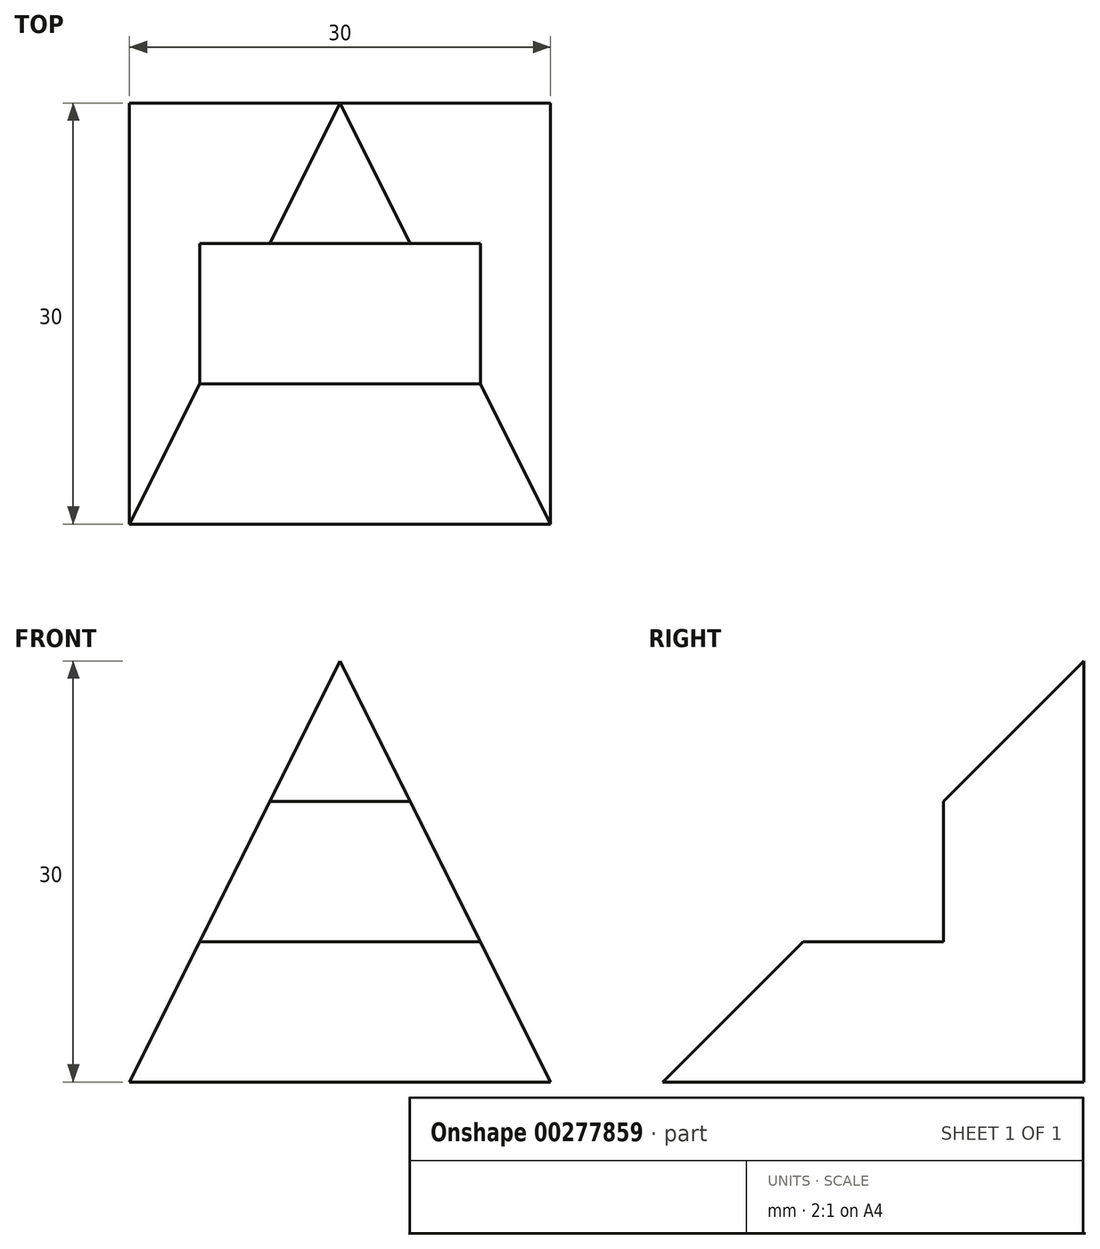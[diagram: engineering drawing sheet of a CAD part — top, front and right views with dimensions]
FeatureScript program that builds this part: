
annotation { "Feature Type Name" : "Feature", "Feature Type Description" : "" }
export const myFeature = defineFeature(function(context is Context, id is Id, definition is map)
    precondition{}
    {
        {
            var Q0;
            Q0=qCreatedBy(makeId("Front.planeOp"),FACE);
            var sketch = newSketch(context, id + "F0", { "sketchPlane" : qUnion([Q0])});
            skLineSegment(sketch, "E0.bottom", {"start": v(-15, 0) * mm, "end": v(15, 0) * mm});
            skLineSegment(sketch, "E0.top", {"start": v(-15, 30) * mm, "end": v(15, 30) * mm});
            skLineSegment(sketch, "E0.left", {"start": v(-15, 0) * mm, "end": v(-15, 30) * mm});
            skLineSegment(sketch, "E0.right", {"start": v(15, 0) * mm, "end": v(15, 30) * mm});
            skLineSegment(sketch, "E1", {"start": v(-15, 0) * mm, "end": v(0, 30) * mm});
            skLineSegment(sketch, "E2", {"start": v(0, 30) * mm, "end": v(15, 0) * mm});
            skSolve(sketch);
        }
        {
            var Q0;
            Q0=makeQuery(id+"F0.imprint","IMPRINT",FACE,{"disambiguationData":[TD([[makeQuery(id+"F0.imprint","IMPRINT",EDGE,{"derivedFrom":sQuery(id+"F0.wireOp",EDGE,"E0.bottom")}),1.0]])]});
            extrude(context, id + "F1", {"entities" : qUnion([Q0]), "depth" : 30 * mm});
        }
        {
            var Q0;
            Q0=qCreatedBy(makeId("Right.planeOp"),FACE);
            var sketch = newSketch(context, id + "F2", { "sketchPlane" : qUnion([Q0])});
            skLineSegment(sketch, "E3.0", {"start": v(-30, 30) * mm, "end": v(0, 30) * mm});
            skLineSegment(sketch, "E4.0", {"start": v(-30, 30) * mm, "end": v(-30, 0) * mm});
            skLineSegment(sketch, "E5", {"start": v(0, 30) * mm, "end": v(-30, 0) * mm});
            skLineSegment(sketch, "E6.bottom", {"start": v(-20, 10) * mm, "end": v(-10, 10) * mm});
            skLineSegment(sketch, "E6.top", {"start": v(-20, 20) * mm, "end": v(-10, 20) * mm});
            skLineSegment(sketch, "E6.left", {"start": v(-20, 10) * mm, "end": v(-20, 20) * mm});
            skLineSegment(sketch, "E6.right", {"start": v(-10, 10) * mm, "end": v(-10, 20) * mm});
            skSolve(sketch);
        }
        {
            var Q0;
            {var subQ3=sQuery(id+"F2.wireOp",EDGE,"E3.0");Q0=makeQuery(id+"F2.imprint","IMPRINT",FACE,{"disambiguationData":[TD([[makeQuery(id+"F2.imprint","IMPRINT",EDGE,{"derivedFrom":subQ3}),-1.0]])]});}
            var Q1;
            {var subQ2=sQuery(id+"F2.wireOp",EDGE,"E6.top");Q1=makeQuery(id+"F2.imprint","IMPRINT",FACE,{"disambiguationData":[TD([[makeQuery(id+"F2.imprint","IMPRINT",EDGE,{"derivedFrom":subQ2}),-1.0]])]});}
            var Q2;
            {var subQ0=sQuery(id+"F2.wireOp",EDGE,"E6.bottom");Q2=makeQuery(id+"F2.imprint","IMPRINT",FACE,{"disambiguationData":[TD([[makeQuery(id+"F2.imprint","IMPRINT",EDGE,{"derivedFrom":subQ0}),1.0]])]});}
            extrude(context, id + "F3", {"entities" : qUnion([Q0, Q1, Q2]), "operationType" : NewBodyOperationType.REMOVE, "oppositeDirection" : true, "depth" : 30 * mm, "symmetric" : true});
        }
    });
